# Revit family: Haworth_Janus_Slant_Table_Dining_Rectangle
name_source: partatom
category: Furniture
revit_build: Autodesk Revit 2018 (Build: 20170223_1515(x64)
units: mm (PartAtom-declared; Revit-internal decimal feet)

## family parameters
Always vertical = Yes
Cut with Voids When Loaded = No
OmniClass Number = 23.40.70.14.64.21
OmniClass Title = Systems Furniture
Room Calculation Point = No
Shared = No
Work Plane-Based = No

## types (2) — shared parameters
Actual Depth = 39"
Actual Height = 29 1/2"
Assembly Code = E2020200
Glide Finish = Haworth _ Polymer _ Black
Manufacturer = Haworth
Revision Number = 2
Size = Verify Final Dim. w/ Haworth
Standard Depths = 39
Standard Height = 29.5
Table Thickness = 29 1/8"
Top Finish = Haworth _ Glass _ Frosted
URL = http://www.haworth.com
URL - Product = https://www.haworth.com
Warranty = https://www.haworth.com

## per-type parameters (varying)
| type | Actual Width | Description | Large | Small |
| HCJC-SL-TDQ39-G | 39" | Haworth Janus Slant Square Dining Table | No | Yes |
| HCJC-SL-TDR79-G | 78 3/4" | Haworth Janus Slant Rectangle Dining Table | Yes | No |

note: column(s) folded — value = type name in every type: Model

## geometry (parser evidence)
native form markers: Sweep x2
no freeform markers — native parametric forms only
